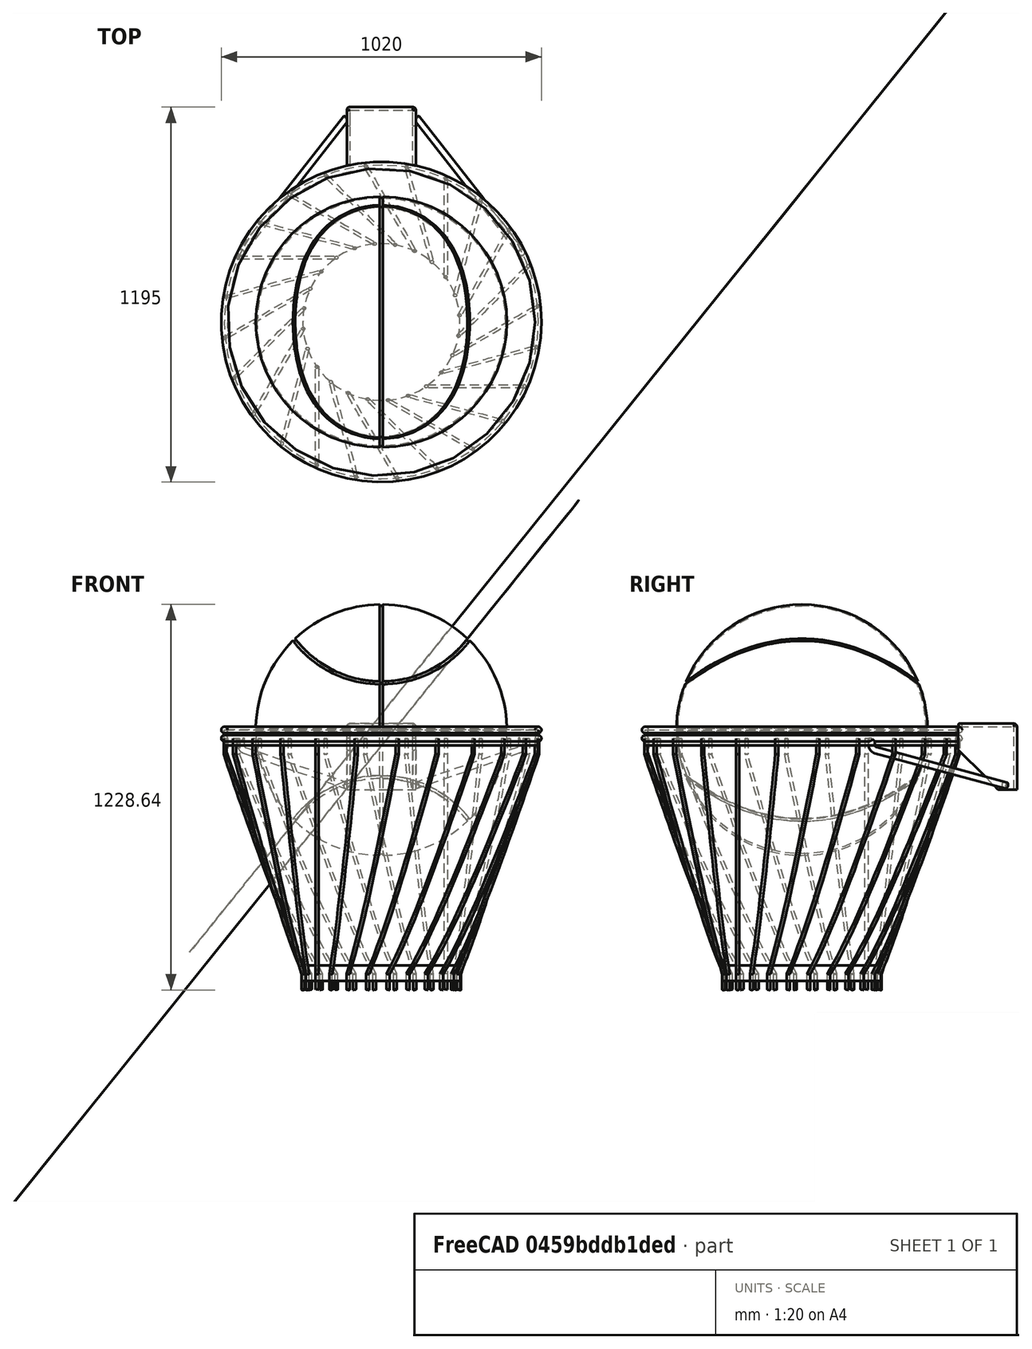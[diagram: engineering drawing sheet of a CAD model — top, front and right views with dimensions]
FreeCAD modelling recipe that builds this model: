
FCSTD DOCUMENT  (FreeCAD 0.18R15419 (Git))
Label: SEXTA BASKET
License: CreativeCommons Attribution-NonCommercial-ShareAlike
LicenseURL: http://creativecommons.org/licenses/by-nc-sa/4.0/
objects: Part::Cut×4, Part::Cylinder×3, Part::Circle×3, Part::Sweep×3, Part::Torus×3, Part::FeaturePython×3, Part::Sphere×2, Part::MultiFuse×2, Sketcher::SketchObject×2, Part::Mirroring×2, Part::Box×1, Part::Chamfer×1, Part::Thickness×1, PartDesign::Revolution×1, PartDesign::Body×1
note: 33 computed .brp shape members not serialized (recipe doc carries the construction recipe); baked Part::Feature solids carry a one-line shape summary decoded from their .brp

FEATURE [Part::Sphere] Sphere
  Angle1 = -90
  Angle2 = 90
  Angle3 = 360
  AttacherType = Attacher::AttachEngine3D
  Radius = 400
FEATURE [Part::Cylinder] Cylinder
  Angle = 360
  AttacherType = Attacher::AttachEngine3D
  Height = 1000
  Placement = pos=(500,0,-497.11) rot=(0,0,1;0rad)
  Radius = 350
FEATURE [Part::Cut] Cut
  Base = -> Sphere
  Tool = -> Cylinder
FEATURE [Part::Circle] Circle
  Angle0 = 0
  Angle1 = 360
  AttacherType = Attacher::AttachEngine3D
  Placement = pos=(150.01,8.2e-14,370.83) rot=(1,0,0;1.5708rad)
  Radius = 5
FEATURE [Part::Sweep] Sweep
  Frenet = true
  Sections = -> [Circle]
  Solid = true
  Spine = -> Cut [Edge2,Edge5,Edge6]
  Transition = 0
FEATURE [Part::Sphere] Sphere001
  Angle1 = -90
  Angle2 = 90
  Angle3 = 360
  AttacherType = Attacher::AttachEngine3D
  Radius = 400
FEATURE [Part::Torus] Torus
  Angle1 = -180
  Angle2 = 180
  Angle3 = 360
  AttacherType = Attacher::AttachEngine3D
  Placement = pos=(0,0,0) rot=(1,0,0;1.5708rad)
  Radius1 = 400
  Radius2 = 5
FEATURE [Part::FeaturePython] Clone  label="Sweep001"  # Draft clone (typed FeaturePython)
  AttacherType = Attacher::AttachEngine3D
  Fuse = false
  Objects = -> [Sweep]
  Placement = pos=(0,0,0) rot=(0,0,1;3.14159rad)
  Scale = (1,1,1)
FEATURE [Part::FeaturePython] Clone001  label="Torus001"  # Draft clone (typed FeaturePython)
  AttacherType = Attacher::AttachEngine3D
  Fuse = false
  Objects = -> [Torus]
  Placement = pos=(0,0,0) rot=(0.57735,0.57735,0.57735;2.0944rad)
  Scale = (1,1,1)
FEATURE [Part::MultiFuse] Fusion
  Shapes = -> [Clone001,Clone,Torus,Sweep]
FEATURE [Part::Cut] Cut001
  Base = -> Sphere001
  Placement = pos=(0,0,0) rot=(0.57735,-0.57735,0.57735;2.0944rad)
  Tool = -> Fusion
FEATURE [Part::Torus] Torus001  label="Torus002"
  Angle1 = -180
  Angle2 = 180
  Angle3 = 360
  AttacherType = Attacher::AttachEngine3D
  Radius1 = 500
  Radius2 = 10
FEATURE [Part::Torus] Torus002  label="Torus003"
  Angle1 = -180
  Angle2 = 180
  Angle3 = 360
  AttacherType = Attacher::AttachEngine3D
  Placement = pos=(0,0,-26.79) rot=(0,0,1;0rad)
  Radius1 = 500
  Radius2 = 10
FEATURE [Part::Box] Box  label="Cube"
  AttacherType = Attacher::AttachEngine3D
  Height = 200
  Length = 200
  Placement = pos=(-100,475,-190) rot=(0,0,1;0rad)
  Width = 200
FEATURE [Part::Chamfer] Chamfer
  Base = -> Box
  Edges = 1 edges r=150: [Edge9]
FEATURE [Part::Thickness] Thickness
  Faces = -> Chamfer [Face2,Face3,Face5]
  Intersection = false
  Join = 0
  Mode = 0
  SelfIntersection = false
  Value = 10
FEATURE [Part::Cylinder] Cylinder001
  Angle = 360
  AttacherType = Attacher::AttachEngine3D
  Height = 100
  Placement = pos=(0,0,-70) rot=(0,0,1;0rad)
  Radius = 510
FEATURE [Part::Cut] Cut002
  Base = -> Thickness
  Tool = -> Cylinder001
FEATURE [Sketcher::SketchObject] Sketch
  MapMode = 5
  Placement = pos=(0,0,0) rot=(0.57735,0.57735,0.57735;2.0944rad)
  Support = -> [YZ_Plane]
  sketch-geometry (3):
    g0: LineSegment StartX=0 StartY=0 StartZ=0 EndX=0 EndY=-20 EndZ=0
    g1: ArcOfCircle CenterX=20 CenterY=-20 CenterZ=0 NormalX=0 NormalY=0 NormalZ=1 AngleXU=0 Radius=20 StartAngle=3.14159 EndAngle=4.50295
    g2: LineSegment StartX=15.8418 StartY=-39.563 StartZ=0 EndX=544.041 EndY=-151.835 EndZ=0
  constraints (8):
    c: Coincident(g-1,g0)
    c: Vertical(g0)
    c: Tangent(g0,g1) = -1.5708
    c: Tangent(g1,g2) = -1.5708
    c: Radius(g1) = 20
    c: DistanceY(g0,g0) = 20
    c: Angle(g2,g-1) = 0.20944
    c: Distance(g2) = 540
FEATURE [Part::Circle] Circle001
  Angle0 = 0
  Angle1 = 360
  AttacherType = Attacher::AttachEngine3D
  Radius = 10
FEATURE [Part::Sweep] Sweep001  label="Sweep002"
  Frenet = true
  Placement = pos=(446.986,221.551,-25) rot=(0,0,1;0.663225rad)
  Sections = -> [Circle001]
  Solid = true
  Spine = -> Sketch [Edge1,Edge2,Edge3]
  Transition = 1
FEATURE [Part::Mirroring] Part__Mirroring  label="Sweep002 (Mirror #1)"
  Base = (0,0,0)
  Normal = (1,0,0)
  Source = -> Sweep001
FEATURE [Part::MultiFuse] Fusion001
  Shapes = -> [Part__Mirroring,Sweep001,Cut002,Torus002,Torus001]
FEATURE [Sketcher::SketchObject] Sketch001
  MapMode = 5
  Placement = pos=(0,0,0) rot=(0.57735,0.57735,0.57735;2.0944rad)
  Support = -> [YZ_Plane]
  sketch-geometry (6):
    g0: LineSegment StartX=0 StartY=0 StartZ=0 EndX=0 EndY=-800 EndZ=0
    g1: LineSegment StartX=0 StartY=-800 StartZ=0 EndX=-250 EndY=-800 EndZ=0
    g2: LineSegment StartX=-250 StartY=-800 StartZ=0 EndX=-250 EndY=-750 EndZ=0
    g3: LineSegment StartX=-250 StartY=-750 StartZ=0 EndX=-500 EndY=-50 EndZ=0
    g4: LineSegment StartX=-500 StartY=-50 StartZ=0 EndX=-500 EndY=0 EndZ=0
    g5: LineSegment StartX=-500 StartY=0 StartZ=0 EndX=0 EndY=0 EndZ=0
  constraints (17):
    c: Coincident(g-1,g0)
    c: Vertical(g0)
    c: Coincident(g0,g1)
    c: Horizontal(g1)
    c: Coincident(g1,g2)
    c: Coincident(g2,g3)
    c: Coincident(g3,g4)
    c: Vertical(g4)
    c: Coincident(g4,g5)
    c: Coincident(g5,g0)
    c: Horizontal(g5)
    c: Vertical(g2)
    c: DistanceX(g5,g5) = 500
    c: DistanceX(g1,g1) = 250
    c: DistanceY(g4,g4) = 50
    c: DistanceY(g2,g2) = 50
    c: DistanceY(g0,g0) = 800
FEATURE [PartDesign::Revolution] Revolution
  Angle = 360
  Axis = (-2e-16,3e-16,1)
  Base = (0,0,0)
  Placement = pos=(0,0,0) rot=(0.57735,0.57735,0.57735;2.0944rad)
  Profile = -> Sketch001
  ReferenceAxis = -> Sketch001 [V_Axis]
FEATURE [PartDesign::Body] Body
  Group = -> [Sketch,Sketch001,Revolution]
  Origin = -> Origin
  Tip = -> Revolution
FEATURE [Part::Cylinder] Cylinder002
  Angle = 360
  AttacherType = Attacher::AttachEngine3D
  Height = 500
  Placement = pos=(205,0,4.55e-14) rot=(0,1,0;1.5708rad)
  Radius = 1000
FEATURE [Part::Cut] Cut003
  Base = -> Revolution
  Tool = -> Cylinder002
FEATURE [Part::Circle] Circle002
  Angle0 = 0
  Angle1 = 360
  AttacherType = Attacher::AttachEngine3D
  Placement = pos=(205,-456.07,0) rot=(0,0,1;0rad)
  Radius = 5
FEATURE [Part::Sweep] Sweep002  label="Sweep003"
  Frenet = true
  Placement = pos=(0,0,-27.75) rot=(0,0,1;0.523599rad)
  Sections = -> [Circle002]
  Solid = true
  Spine = -> Cut003 [Edge8,Edge7,Edge6]
  Transition = 0
FEATURE [Part::FeaturePython] Array  # Draft array (typed FeaturePython)
  Angle = 360
  ArrayType = 1
  Axis = (0,0,1)
  Base = -> Sweep002
  Center = (0,0,0)
  Fuse = false
  IntervalAxis = (0,0,0)
  IntervalX = (1,0,0)
  IntervalY = (0,1,0)
  IntervalZ = (0,0,1)
  NumberPolar = 24
  NumberX = 2
  NumberY = 2
  NumberZ = 1
FEATURE [Part::Mirroring] Part__Mirroring001  label="Array (Mirror #2)"
  Base = (0,0,0)
  Normal = (1,0,0)
  Source = -> Array
